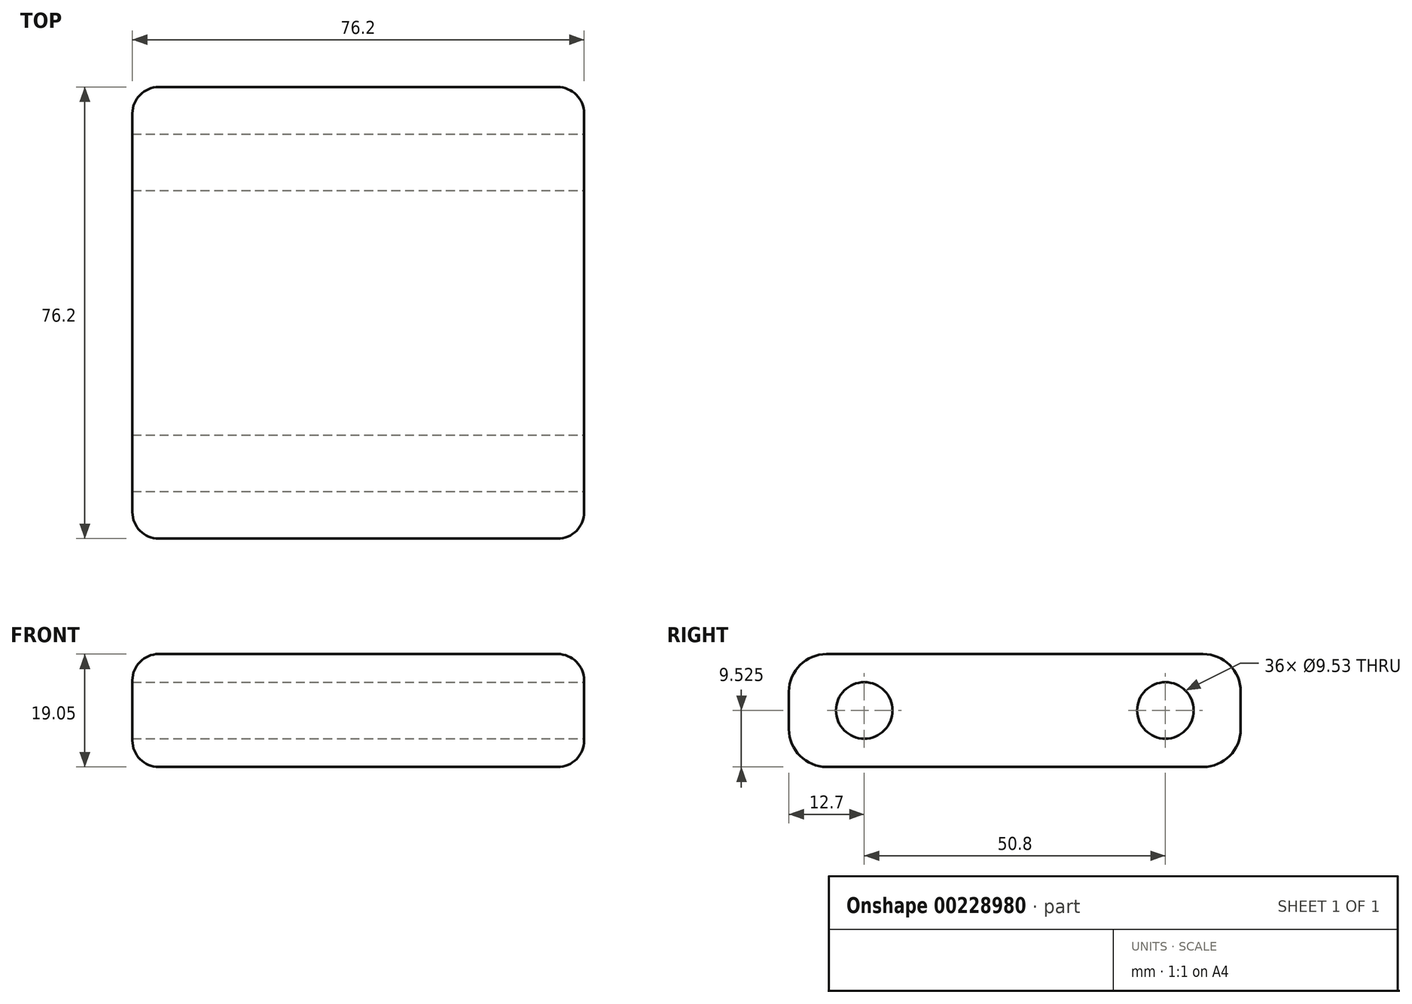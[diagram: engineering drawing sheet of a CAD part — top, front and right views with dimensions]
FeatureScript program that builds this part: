
annotation { "Feature Type Name" : "Feature", "Feature Type Description" : "" }
export const myFeature = defineFeature(function(context is Context, id is Id, definition is map)
    precondition{}
    {
        {
            var Q0;
            Q0=qCreatedBy(makeId("Top.planeOp"),FACE);
            var sketch = newSketch(context, id + "F0", { "sketchPlane" : qUnion([Q0])});
            skLineSegment(sketch, "E0.bottom", {"start": v(38.1, 38.1) * mm, "end": v(-38.1, 38.1) * mm});
            skLineSegment(sketch, "E0.top", {"start": v(38.1, -38.1) * mm, "end": v(-38.1, -38.1) * mm});
            skLineSegment(sketch, "E0.left", {"start": v(38.1, 38.1) * mm, "end": v(38.1, -38.1) * mm});
            skLineSegment(sketch, "E0.right", {"start": v(-38.1, 38.1) * mm, "end": v(-38.1, -38.1) * mm});
            skPoint(sketch, "E0.middle", {"position": v(0, 0) * mm});
            skSolve(sketch);
        }
        {
            var Q0;
            Q0 = qSketchRegion(id + "F0", true);
            extrude(context, id + "F1", {"entities" : qUnion([Q0]), "depth" : 19.05 * mm});
        }
        {
            var Q0;
            Q0=makeQuery(id+"F1.opExtrude","SWEPT_FACE",FACE,{"disambiguationData":[OSD([sQuery(id+"F0.wireOp",EDGE,"E0.right")])]});
            var sketch = newSketch(context, id + "F2", { "sketchPlane" : qUnion([Q0])});
            skPoint(sketch, "E1.endSnap0", {"position": v(38.1, 9.53) * mm});
            skPoint(sketch, "E2", {"position": v(-25.4, 9.53) * mm});
            skPoint(sketch, "E3", {"position": v(25.4, 9.53) * mm});
            skSolve(sketch);
        }
        {
            var Q0;
            Q0=sQuery(id+"F2.wireOp",VERTEX,"E2");
            var Q1;
            Q1=sQuery(id+"F2.wireOp",VERTEX,"E3");
            var Q2;
            Q2=makeQuery(id+"F1.opExtrude","SWEPT_BODY",BODY,{"disambiguationData":[OSD([sQuery(id+"F0.wireOp",EDGE,"E0.bottom"),sQuery(id+"F0.wireOp",EDGE,"E0.top"),sQuery(id+"F0.wireOp",EDGE,"E0.left"),sQuery(id+"F0.wireOp",EDGE,"E0.right")])]});
            hole(context, id + "F3", {"style" : HoleStyle.SIMPLE, "endStyle" : HoleEndStyle.THROUGH, "holeDiameter" : 9.52 * mm, "locations" : qUnion([Q0, Q1]), "scope" : qUnion([Q2]), "isTappedThrough" : true, "startStyle" : HoleStartStyle.SKETCH});
        }
        {
            var Q0;
            Q0=makeQuery(id+"F1.opExtrude","CAP_EDGE",EDGE,{"disambiguationData":[OSD([sQuery(id+"F0.wireOp",EDGE,"E0.top")])],"isStart":false});
            var Q1;
            Q1=makeQuery(id+"F1.opExtrude","CAP_EDGE",EDGE,{"disambiguationData":[OSD([sQuery(id+"F0.wireOp",EDGE,"E0.top")])],"isStart":true});
            var Q2;
            Q2=makeQuery(id+"F1.opExtrude","CAP_EDGE",EDGE,{"disambiguationData":[OSD([sQuery(id+"F0.wireOp",EDGE,"E0.bottom")])],"isStart":false});
            var Q3;
            Q3=makeQuery(id+"F1.opExtrude","CAP_EDGE",EDGE,{"disambiguationData":[OSD([sQuery(id+"F0.wireOp",EDGE,"E0.bottom")])],"isStart":true});
            fillet(context, id + "F4", {"entities" : qUnion([Q0, Q1, Q2, Q3]), "radius" : 6.35 * mm, "tangentPropagation" : true, "allowEdgeOverflow" : false});
        }
        {
            var Q0;
            Q0=makeQuery(id+"F1.opExtrude","CAP_EDGE",EDGE,{"disambiguationData":[OSD([sQuery(id+"F0.wireOp",EDGE,"E0.right")])],"isStart":false});
            var Q1;
            Q1=makeQuery(id+"F1.opExtrude","CAP_EDGE",EDGE,{"disambiguationData":[OSD([sQuery(id+"F0.wireOp",EDGE,"E0.left")])],"isStart":false});
            fillet(context, id + "F5", {"entities" : qUnion([Q0, Q1]), "radius" : 4.44 * mm, "tangentPropagation" : true, "allowEdgeOverflow" : false});
        }
    });
